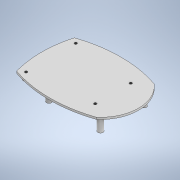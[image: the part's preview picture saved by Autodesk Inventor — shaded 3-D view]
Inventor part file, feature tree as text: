
AUTODESK INVENTOR PART (.ipt)
format: ipt  version: 2021 (Build 250183000, 183)  size: 885,760 bytes
history: native  units: mm
features: sketch x7, other x4, extrude x3, plane x1
ambient origin geometry x8: Origin, YZ Plane, XZ Plane, XY Plane, X Axis, Y Axis, Z Axis, Center Point
bodies: Volumenkörper1 (feature_tree)
feature tree (15):
  sketch  "Skizze4"  dims[d33=56.0mm]
  sketch  "Skizze3"  dims[d31=58.0mm d32=49.0mm]
  extrude  "Extrusion1"  Depth=5.8mm
  extrude  "Extrusion2"  Depth=90.0mm
  extrude  "Extrusion3"  Depth=49.0mm
  plane  "Arbeitsebene1"
  sketch  "Skizze6"  dims[d34=40.0mm]
  other  "Spirale1"
  other  "Spirale2"
  sketch  "Skizzenbasierte Anordnung1"  dims[d19=2.512875mm d20=5.8mm]
  sketch  "Skizzenbasierte Anordnung2"  dims[d28=80.0mm d30=90.0mm]
  other  "Arbeitsachse1"
  other  "Arbeitsachse2"
  sketch  "Skizze7"  dims[d35=70.0mm]
  sketch  "Skizze8"  dims[d36=65.0mm d37=65.0mm d38=22.47mm d39=120.0mm d40=6.0mm d41=2.512875mm d42=43.0mm d43=2.2mm d44=0.0mm d45=17.0mm d46=0.0mm d47=60.0deg d48=3.0mm d49=0.45mm d50=2.512875mm d51=0.243562mm d52=0.048713mm d53=60.0deg d54=3.0mm d55=0.45mm d56=2.512875mm d57=0.3897mm d58=6.0mm d59=5.0mm d60=0.0mm d62=0.0mm d63=0.45mm d64=10.0mm d65=10.0mm d66=0.0mm d67=90.0deg d68=90.0deg d69=0.0mm d70=0.0mm d71=60.0deg d72=3.0mm d73=0.45mm d74=2.512875mm d75=0.243563mm d76=0.048713mm d77=60.0deg d78=3.0mm d79=0.45mm d80=2.512875mm d81=0.3897mm d82=0.0mm d83=0.45mm d84=10.0mm d85=10.0mm d86=0.0mm d87=90.0deg d88=90.0deg d89=0.0mm d90=0.0mm]
